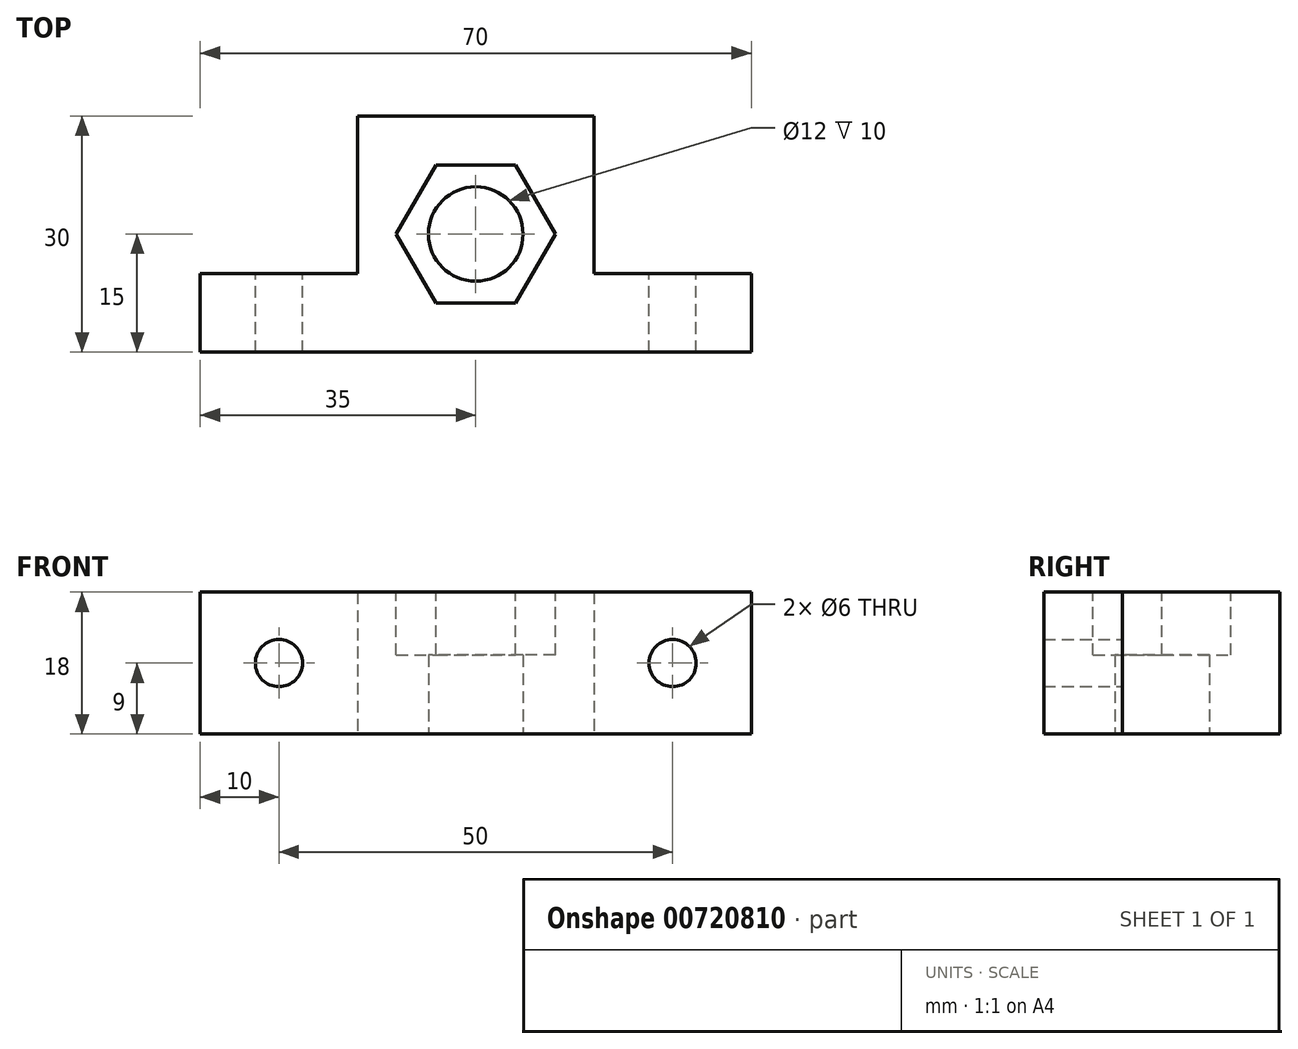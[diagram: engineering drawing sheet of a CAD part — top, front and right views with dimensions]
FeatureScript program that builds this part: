
annotation { "Feature Type Name" : "Feature", "Feature Type Description" : "" }
export const myFeature = defineFeature(function(context is Context, id is Id, definition is map)
    precondition{}
    {
        {
            var Q0;
            Q0=qCreatedBy(makeId("Top.planeOp"),FACE);
            var sketch = newSketch(context, id + "F0", { "sketchPlane" : qUnion([Q0])});
            skPoint(sketch, "E0.0", {"position": v(0, 0) * mm});
            skLineSegment(sketch, "E1.bottom", {"start": v(0, 0) * mm, "end": v(70, 0) * mm});
            skLineSegment(sketch, "E1.top", {"start": v(20, 30) * mm, "end": v(50, 30) * mm});
            skLineSegment(sketch, "E1.left", {"start": v(0, 0) * mm, "end": v(0, 10) * mm});
            skLineSegment(sketch, "E1.right", {"start": v(70, 0) * mm, "end": v(70, 10) * mm});
            skLineSegment(sketch, "E2.top", {"start": v(0, 10) * mm, "end": v(20, 10) * mm});
            skLineSegment(sketch, "E2.right", {"start": v(20, 30) * mm, "end": v(20, 10) * mm});
            skLineSegment(sketch, "E3.top", {"start": v(70, 10) * mm, "end": v(50, 10) * mm});
            skLineSegment(sketch, "E3.right", {"start": v(50, 30) * mm, "end": v(50, 10) * mm});
            skCircle(sketch, "E4", {"center": v(35, 15) * mm, "radius": 6 * mm});
            skPoint(sketch, "E4.centerSnap0", {"position": v(35, 0) * mm});
            skSolve(sketch);
        }
        {
            var Q0;
            Q0=makeQuery(id+"F0.imprint","IMPRINT",FACE,{"disambiguationData":[TD([[makeQuery(id+"F0.imprint","IMPRINT",EDGE,{"derivedFrom":sQuery(id+"F0.wireOp",EDGE,"E1.bottom")}),1.0]])]});
            extrude(context, id + "F1", {"entities" : qUnion([Q0]), "depth" : 18 * mm, "offsetDistance" : 25 * mm});
        }
        {
            var Q0;
            Q0=makeQuery(id+"F1.opExtrude","CAP_FACE",FACE,{"disambiguationData":[OSD([sQuery(id+"F0.wireOp",EDGE,"E1.bottom"),sQuery(id+"F0.wireOp",EDGE,"E1.top"),sQuery(id+"F0.wireOp",EDGE,"E1.left"),sQuery(id+"F0.wireOp",EDGE,"E1.right"),sQuery(id+"F0.wireOp",EDGE,"E2.top"),sQuery(id+"F0.wireOp",EDGE,"E2.right"),sQuery(id+"F0.wireOp",EDGE,"E3.top"),sQuery(id+"F0.wireOp",EDGE,"E3.right"),sQuery(id+"F0.wireOp",EDGE,"E4")])],"isStart":false});
            var sketch = newSketch(context, id + "F2", { "sketchPlane" : qUnion([Q0])});
            skCircle(sketch, "E5.cCircle", {"center": v(35, 15) * mm, "radius": 8.75 * mm, "construction": true});
            skLineSegment(sketch, "E5.0", {"start": v(29.95, 23.75) * mm, "end": v(40.05, 23.75) * mm});
            skLineSegment(sketch, "E5.1", {"start": v(40.05, 23.75) * mm, "end": v(45.1, 15) * mm});
            skLineSegment(sketch, "E5.2", {"start": v(45.1, 15) * mm, "end": v(40.05, 6.25) * mm});
            skLineSegment(sketch, "E5.3", {"start": v(40.05, 6.25) * mm, "end": v(29.95, 6.25) * mm});
            skLineSegment(sketch, "E5.4", {"start": v(29.95, 6.25) * mm, "end": v(24.9, 15) * mm});
            skLineSegment(sketch, "E5.5", {"start": v(24.9, 15) * mm, "end": v(29.95, 23.75) * mm});
            skPoint(sketch, "E5.0.midPoint", {"position": v(35, 23.75) * mm});
            skSolve(sketch);
        }
        {
            var Q0;
            Q0=makeQuery(id+"F2.imprint","IMPRINT",FACE,{"disambiguationData":[TD([[makeQuery(id+"F2.imprint","IMPRINT",EDGE,{"derivedFrom":sQuery(id+"F2.wireOp",EDGE,"E5.0")}),-1.0]])]});
            extrude(context, id + "F3", {"entities" : qUnion([Q0]), "operationType" : NewBodyOperationType.REMOVE, "oppositeDirection" : true, "depth" : 8 * mm, "offsetDistance" : 25 * mm});
        }
        {
            var Q0;
            Q0=makeQuery(id+"F1.opExtrude","SWEPT_FACE",FACE,{"disambiguationData":[OSD([sQuery(id+"F0.wireOp",EDGE,"E3.top")])]});
            var sketch = newSketch(context, id + "F4", { "sketchPlane" : qUnion([Q0])});
            skCircle(sketch, "E6", {"center": v(-60, 9) * mm, "radius": 3 * mm});
            skPoint(sketch, "E6.centerSnap0", {"position": v(-70, 9) * mm});
            skCircle(sketch, "E7", {"center": v(-10, 9) * mm, "radius": 3 * mm});
            skSolve(sketch);
        }
        {
            var Q0;
            Q0=makeQuery(id+"F4.imprint","IMPRINT",FACE,{"disambiguationData":[TD([[makeQuery(id+"F4.imprint","IMPRINT",EDGE,{"derivedFrom":sQuery(id+"F4.wireOp",EDGE,"E6")}),1.0]])]});
            var Q1;
            Q1=makeQuery(id+"F4.imprint","IMPRINT",FACE,{"disambiguationData":[TD([[makeQuery(id+"F4.imprint","IMPRINT",EDGE,{"derivedFrom":sQuery(id+"F4.wireOp",EDGE,"E7")}),1.0]])]});
            extrude(context, id + "F5", {"entities" : qUnion([Q0, Q1]), "operationType" : NewBodyOperationType.REMOVE, "oppositeDirection" : true, "depth" : 25 * mm, "offsetDistance" : 25 * mm});
        }
    });
